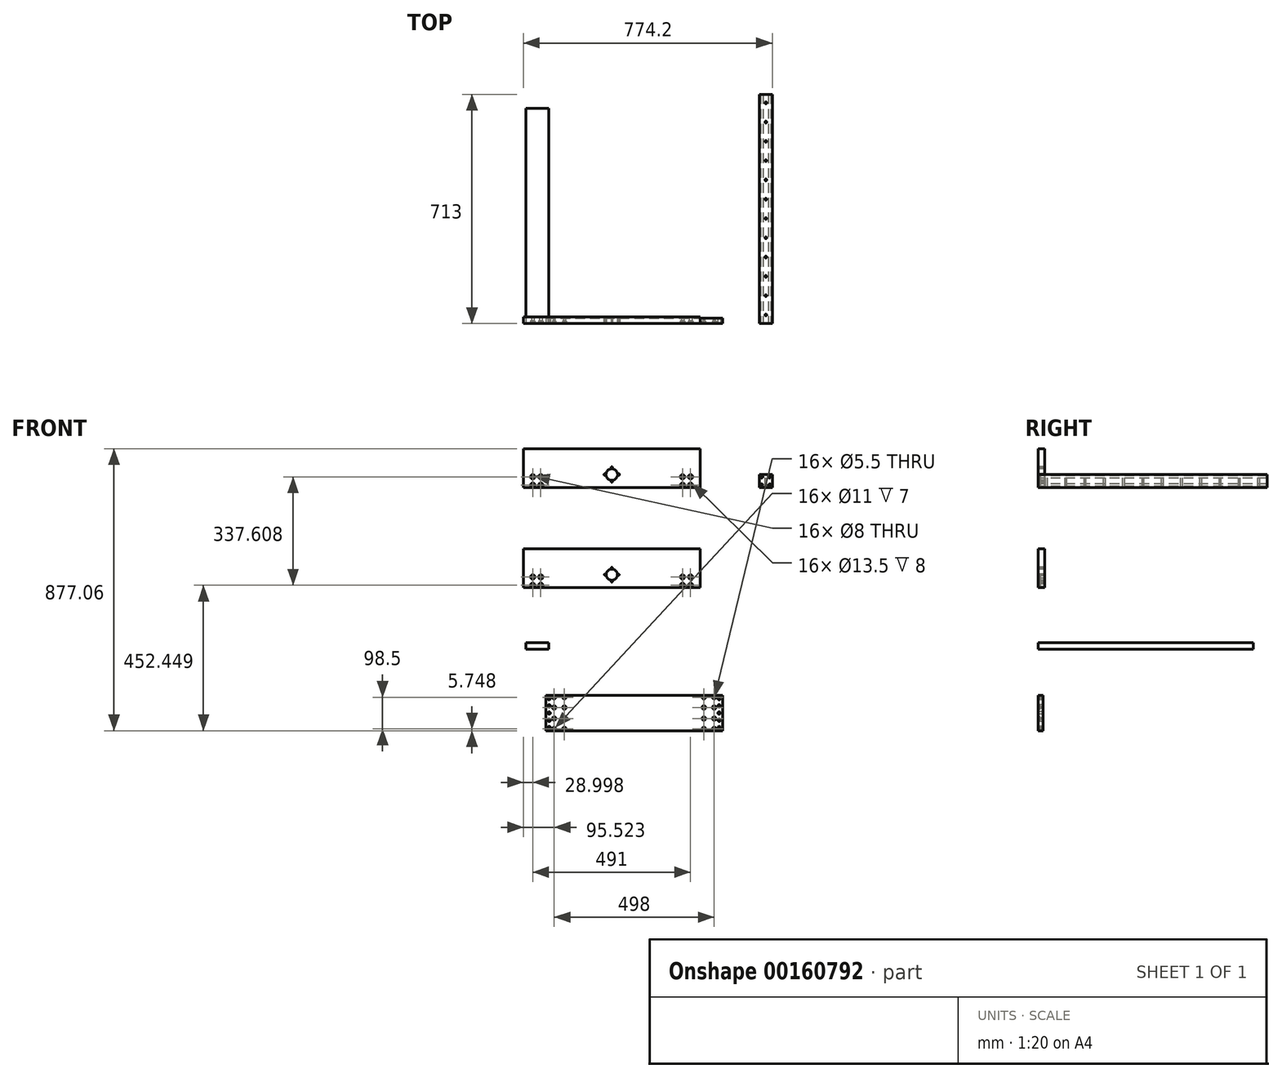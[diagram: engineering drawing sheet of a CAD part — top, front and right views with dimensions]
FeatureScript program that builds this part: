
annotation { "Feature Type Name" : "Feature", "Feature Type Description" : "" }
export const myFeature = defineFeature(function(context is Context, id is Id, definition is map)
    precondition{}
    {
        {
            var Q0;
            Q0=qCreatedBy(makeId("Front.planeOp"),FACE);
            var sketch = newSketch(context, id + "F0", { "sketchPlane" : qUnion([Q0])});
            skLineSegment(sketch, "E0.bottom", {"start": v(-1050.56, 346.5) * mm, "end": v(-500.56, 346.5) * mm});
            skLineSegment(sketch, "E0.top", {"start": v(-1050.56, 226.5) * mm, "end": v(-500.56, 226.5) * mm});
            skLineSegment(sketch, "E0.left", {"start": v(-1050.56, 346.5) * mm, "end": v(-1050.56, 226.5) * mm});
            skLineSegment(sketch, "E0.right", {"start": v(-500.56, 346.5) * mm, "end": v(-500.56, 226.5) * mm});
            skLineSegment(sketch, "E1.bottom", {"start": v(-316.36, 266.5) * mm, "end": v(-276.36, 266.5) * mm});
            skLineSegment(sketch, "E1.top", {"start": v(-316.36, 226.5) * mm, "end": v(-276.36, 226.5) * mm});
            skLineSegment(sketch, "E1.left", {"start": v(-316.36, 266.5) * mm, "end": v(-316.36, 226.5) * mm});
            skLineSegment(sketch, "E1.right", {"start": v(-276.36, 266.5) * mm, "end": v(-276.36, 226.5) * mm});
            skCircle(sketch, "E2", {"center": v(-309.36, 259.5) * mm, "radius": 4 * mm});
            skCircle(sketch, "E3.0.1.0", {"center": v(-309.36, 233.5) * mm, "radius": 4 * mm});
            skCircle(sketch, "E3.1.0.0", {"center": v(-284.36, 259.5) * mm, "radius": 4 * mm});
            skCircle(sketch, "E3.1.1.0", {"center": v(-284.36, 233.5) * mm, "radius": 4 * mm});
            skLineSegment(sketch, "E3.direction1", {"start": v(-309.36, 259.5) * mm, "end": v(-284.36, 259.5) * mm, "construction": true});
            skLineSegment(sketch, "E3.direction2", {"start": v(-309.36, 259.5) * mm, "end": v(-309.36, 233.5) * mm, "construction": true});
            skCircle(sketch, "E4.1.1.0", {"center": v(-142.75, 136.48) * mm, "radius": 4 * mm});
            skLineSegment(sketch, "E5.0", {"start": v(-1028.56, 346.5) * mm, "end": v(-1028.56, 226.5) * mm, "construction": true});
            skLineSegment(sketch, "E6.0", {"start": v(-522.56, 346.5) * mm, "end": v(-522.56, 226.5) * mm, "construction": true});
            skLineSegment(sketch, "E7.0", {"start": v(-1050.56, 266.5) * mm, "end": v(-500.56, 266.5) * mm, "construction": true});
            skLineSegment(sketch, "E8.bottom", {"start": v(-1028.56, 266.5) * mm, "end": v(-988.56, 266.5) * mm, "construction": true});
            skLineSegment(sketch, "E8.top", {"start": v(-1028.56, 226.5) * mm, "end": v(-988.56, 226.5) * mm, "construction": true});
            skLineSegment(sketch, "E8.left", {"start": v(-1028.56, 266.5) * mm, "end": v(-1028.56, 226.5) * mm, "construction": true});
            skLineSegment(sketch, "E8.right", {"start": v(-988.56, 266.5) * mm, "end": v(-988.56, 226.5) * mm, "construction": true});
            skCircle(sketch, "E9", {"center": v(-1021.56, 259.5) * mm, "radius": 4 * mm, "construction": true});
            skCircle(sketch, "E10.0.1.0", {"center": v(-1021.56, 233.5) * mm, "radius": 4 * mm, "construction": true});
            skCircle(sketch, "E10.1.0.0", {"center": v(-996.56, 259.5) * mm, "radius": 4 * mm, "construction": true});
            skCircle(sketch, "E10.1.1.0", {"center": v(-996.56, 233.5) * mm, "radius": 4 * mm, "construction": true});
            skLineSegment(sketch, "E10.direction1", {"start": v(-1021.56, 259.5) * mm, "end": v(-996.56, 259.5) * mm, "construction": true});
            skLineSegment(sketch, "E10.direction2", {"start": v(-1021.56, 259.5) * mm, "end": v(-1021.56, 233.5) * mm, "construction": true});
            skLineSegment(sketch, "E11.bottom", {"start": v(-562.56, 266.5) * mm, "end": v(-522.56, 266.5) * mm, "construction": true});
            skLineSegment(sketch, "E11.top", {"start": v(-562.56, 226.5) * mm, "end": v(-522.56, 226.5) * mm, "construction": true});
            skLineSegment(sketch, "E11.left", {"start": v(-562.56, 266.5) * mm, "end": v(-562.56, 226.5) * mm, "construction": true});
            skLineSegment(sketch, "E11.right", {"start": v(-522.56, 266.5) * mm, "end": v(-522.56, 226.5) * mm, "construction": true});
            skCircle(sketch, "E12", {"center": v(-555.56, 259.5) * mm, "radius": 4 * mm, "construction": true});
            skCircle(sketch, "E13.0.1.0", {"center": v(-555.56, 233.5) * mm, "radius": 4 * mm, "construction": true});
            skCircle(sketch, "E13.1.0.0", {"center": v(-530.56, 259.5) * mm, "radius": 4 * mm, "construction": true});
            skCircle(sketch, "E13.1.1.0", {"center": v(-530.56, 233.5) * mm, "radius": 4 * mm, "construction": true});
            skLineSegment(sketch, "E13.direction1", {"start": v(-555.56, 259.5) * mm, "end": v(-530.56, 259.5) * mm, "construction": true});
            skLineSegment(sketch, "E13.direction2", {"start": v(-555.56, 259.5) * mm, "end": v(-555.56, 233.5) * mm, "construction": true});
            skLineSegment(sketch, "E14.bottom", {"start": v(-1050.56, 34.9) * mm, "end": v(-500.56, 34.9) * mm});
            skLineSegment(sketch, "E14.top", {"start": v(-1050.56, -85.1) * mm, "end": v(-500.56, -85.1) * mm});
            skLineSegment(sketch, "E14.left", {"start": v(-1050.56, 34.9) * mm, "end": v(-1050.56, -85.1) * mm});
            skLineSegment(sketch, "E14.right", {"start": v(-500.56, 34.9) * mm, "end": v(-500.56, -85.1) * mm});
            skLineSegment(sketch, "E15.0", {"start": v(-1028.56, 34.9) * mm, "end": v(-1028.56, -85.1) * mm, "construction": true});
            skLineSegment(sketch, "E16.0", {"start": v(-522.56, 34.9) * mm, "end": v(-522.56, -85.1) * mm, "construction": true});
            skLineSegment(sketch, "E17.0", {"start": v(-1050.56, -45.1) * mm, "end": v(-500.56, -45.1) * mm, "construction": true});
            skLineSegment(sketch, "E18.bottom", {"start": v(-1028.56, -45.1) * mm, "end": v(-988.56, -45.1) * mm, "construction": true});
            skLineSegment(sketch, "E18.top", {"start": v(-1028.56, -85.1) * mm, "end": v(-988.56, -85.1) * mm, "construction": true});
            skLineSegment(sketch, "E18.left", {"start": v(-1028.56, -45.1) * mm, "end": v(-1028.56, -85.1) * mm, "construction": true});
            skLineSegment(sketch, "E18.right", {"start": v(-988.56, -45.1) * mm, "end": v(-988.56, -85.1) * mm, "construction": true});
            skCircle(sketch, "E19", {"center": v(-1021.56, -52.1) * mm, "radius": 4 * mm, "construction": true});
            skCircle(sketch, "E20.0.1.0", {"center": v(-1021.56, -78.1) * mm, "radius": 4 * mm, "construction": true});
            skCircle(sketch, "E20.1.0.0", {"center": v(-996.56, -52.1) * mm, "radius": 4 * mm, "construction": true});
            skCircle(sketch, "E20.1.1.0", {"center": v(-996.56, -78.1) * mm, "radius": 4 * mm, "construction": true});
            skLineSegment(sketch, "E20.direction1", {"start": v(-1021.56, -52.1) * mm, "end": v(-996.56, -52.1) * mm, "construction": true});
            skLineSegment(sketch, "E20.direction2", {"start": v(-1021.56, -52.1) * mm, "end": v(-1021.56, -78.1) * mm, "construction": true});
            skLineSegment(sketch, "E21.bottom", {"start": v(-562.56, -45.1) * mm, "end": v(-522.56, -45.1) * mm, "construction": true});
            skLineSegment(sketch, "E21.top", {"start": v(-562.56, -85.1) * mm, "end": v(-522.56, -85.1) * mm, "construction": true});
            skLineSegment(sketch, "E21.left", {"start": v(-562.56, -45.1) * mm, "end": v(-562.56, -85.1) * mm, "construction": true});
            skLineSegment(sketch, "E21.right", {"start": v(-522.56, -45.1) * mm, "end": v(-522.56, -85.1) * mm, "construction": true});
            skCircle(sketch, "E22", {"center": v(-555.56, -52.1) * mm, "radius": 4 * mm, "construction": true});
            skCircle(sketch, "E23.0.1.0", {"center": v(-555.56, -78.1) * mm, "radius": 4 * mm, "construction": true});
            skCircle(sketch, "E23.1.0.0", {"center": v(-530.56, -52.1) * mm, "radius": 4 * mm, "construction": true});
            skCircle(sketch, "E23.1.1.0", {"center": v(-530.56, -78.1) * mm, "radius": 4 * mm, "construction": true});
            skLineSegment(sketch, "E23.direction1", {"start": v(-555.56, -52.1) * mm, "end": v(-530.56, -52.1) * mm, "construction": true});
            skLineSegment(sketch, "E23.direction2", {"start": v(-555.56, -52.1) * mm, "end": v(-555.56, -78.1) * mm, "construction": true});
            skLineSegment(sketch, "E24.bottom", {"start": v(-1042.35, -257.26) * mm, "end": v(-972.35, -257.26) * mm});
            skLineSegment(sketch, "E24.top", {"start": v(-1042.35, -277.26) * mm, "end": v(-972.35, -277.26) * mm});
            skLineSegment(sketch, "E24.left", {"start": v(-1042.35, -257.26) * mm, "end": v(-1042.35, -277.26) * mm});
            skLineSegment(sketch, "E24.right", {"start": v(-972.35, -257.26) * mm, "end": v(-972.35, -277.26) * mm});
            skCircle(sketch, "E25", {"center": v(-1032.35, -267.26) * mm, "radius": 4.21 * mm, "construction": true});
            skCircle(sketch, "E26.1.0.0", {"center": v(-1007.35, -267.26) * mm, "radius": 4.21 * mm, "construction": true});
            skCircle(sketch, "E26.2.0.0", {"center": v(-982.35, -267.26) * mm, "radius": 4.21 * mm, "construction": true});
            skLineSegment(sketch, "E26.direction1", {"start": v(-1032.35, -267.26) * mm, "end": v(-1007.35, -267.26) * mm, "construction": true});
            skLineSegment(sketch, "E27", {"start": v(-775.56, 226.5) * mm, "end": v(-775.56, 346.5) * mm, "construction": true});
            skLineSegment(sketch, "E28", {"start": v(-753.56, 266.5) * mm, "end": v(-775.56, 266.5) * mm, "construction": true});
            skCircle(sketch, "E29", {"center": v(-775.56, 266.5) * mm, "radius": 22 * mm, "construction": true});
            skCircle(sketch, "E30", {"center": v(-753.56, 266.5) * mm, "radius": 2.25 * mm});
            skCircle(sketch, "E31.1.0", {"center": v(-775.56, 288.5) * mm, "radius": 2.25 * mm});
            skCircle(sketch, "E31.2.0", {"center": v(-797.56, 266.5) * mm, "radius": 2.25 * mm});
            skCircle(sketch, "E31.3.0", {"center": v(-775.56, 244.5) * mm, "radius": 2.25 * mm});
            skLineSegment(sketch, "E32", {"start": v(-757.56, 266.5) * mm, "end": v(-775.56, 266.5) * mm, "construction": true});
            skCircle(sketch, "E33", {"center": v(-775.56, 266.5) * mm, "radius": 18 * mm});
            skCircle(sketch, "E34", {"center": v(-775.56, 266.5) * mm, "radius": 8.65 * mm, "construction": true});
            skLineSegment(sketch, "E35", {"start": v(-775.56, 34.9) * mm, "end": v(-775.56, -85.1) * mm, "construction": true});
            skLineSegment(sketch, "E36", {"start": v(-775.56, -24.1) * mm, "end": v(-775.56, -45.1) * mm, "construction": true});
            skLineSegment(sketch, "E37", {"start": v(-792.96, -45.1) * mm, "end": v(-775.56, -45.1) * mm, "construction": true});
            skCircle(sketch, "E38", {"center": v(-775.56, -45.1) * mm, "radius": 21 * mm, "construction": true});
            skCircle(sketch, "E39", {"center": v(-775.56, -45.1) * mm, "radius": 17.4 * mm});
            skCircle(sketch, "E40", {"center": v(-775.56, -24.1) * mm, "radius": 2.25 * mm, "construction": true});
            skCircle(sketch, "E41.1.0", {"center": v(-796.56, -45.1) * mm, "radius": 2.25 * mm, "construction": true});
            skCircle(sketch, "E41.2.0", {"center": v(-775.56, -66.1) * mm, "radius": 2.25 * mm, "construction": true});
            skCircle(sketch, "E41.3.0", {"center": v(-754.56, -45.1) * mm, "radius": 2.25 * mm, "construction": true});
            skLineSegment(sketch, "E42.bottom", {"start": v(-981.04, -420.55) * mm, "end": v(-431.04, -420.55) * mm});
            skLineSegment(sketch, "E42.top", {"start": v(-981.04, -530.55) * mm, "end": v(-431.04, -530.55) * mm});
            skLineSegment(sketch, "E42.left", {"start": v(-981.04, -420.55) * mm, "end": v(-981.04, -530.55) * mm});
            skLineSegment(sketch, "E42.right", {"start": v(-431.04, -420.55) * mm, "end": v(-431.04, -530.55) * mm});
            skLineSegment(sketch, "E43.bottom", {"start": v(-918.04, -542.05) * mm, "end": v(-918.04, -475.55) * mm, "construction": true});
            skLineSegment(sketch, "E43.top", {"start": v(-960.04, -542.05) * mm, "end": v(-960.04, -475.55) * mm, "construction": true});
            skLineSegment(sketch, "E43.right", {"start": v(-918.04, -475.55) * mm, "end": v(-960.04, -475.55) * mm, "construction": true});
            skPoint(sketch, "E43.middle", {"position": v(-939.04, -508.8) * mm});
            skLineSegment(sketch, "E44.bottom", {"start": v(-955.04, -524.8) * mm, "end": v(-955.04, -492.8) * mm, "construction": true});
            skLineSegment(sketch, "E44.top", {"start": v(-923.04, -524.8) * mm, "end": v(-923.04, -492.8) * mm, "construction": true});
            skLineSegment(sketch, "E44.left", {"start": v(-955.04, -524.8) * mm, "end": v(-923.04, -524.8) * mm, "construction": true});
            skLineSegment(sketch, "E44.right", {"start": v(-955.04, -492.8) * mm, "end": v(-923.04, -492.8) * mm, "construction": true});
            skLineSegment(sketch, "E45", {"start": v(-918.04, -542.05) * mm, "end": v(-960.04, -542.05) * mm, "construction": true});
            skCircle(sketch, "E46", {"center": v(-923.04, -524.8) * mm, "radius": 2.75 * mm, "construction": true});
            skCircle(sketch, "E47.1.0", {"center": v(-923.04, -492.8) * mm, "radius": 2.75 * mm, "construction": true});
            skCircle(sketch, "E47.2.0", {"center": v(-955.04, -492.8) * mm, "radius": 2.75 * mm, "construction": true});
            skCircle(sketch, "E47.3.0", {"center": v(-955.04, -524.8) * mm, "radius": 2.75 * mm, "construction": true});
            skLineSegment(sketch, "E48.bottom", {"start": v(-918.04, -475.55) * mm, "end": v(-918.04, -409.05) * mm, "construction": true});
            skLineSegment(sketch, "E48.top", {"start": v(-960.04, -475.55) * mm, "end": v(-960.04, -409.05) * mm, "construction": true});
            skLineSegment(sketch, "E48.right", {"start": v(-918.04, -409.05) * mm, "end": v(-960.04, -409.05) * mm, "construction": true});
            skPoint(sketch, "E48.middle", {"position": v(-939.04, -442.3) * mm});
            skLineSegment(sketch, "E49.bottom", {"start": v(-955.04, -458.3) * mm, "end": v(-955.04, -426.3) * mm, "construction": true});
            skLineSegment(sketch, "E49.top", {"start": v(-923.04, -458.3) * mm, "end": v(-923.04, -426.3) * mm, "construction": true});
            skLineSegment(sketch, "E49.left", {"start": v(-955.04, -458.3) * mm, "end": v(-923.04, -458.3) * mm, "construction": true});
            skLineSegment(sketch, "E49.right", {"start": v(-955.04, -426.3) * mm, "end": v(-923.04, -426.3) * mm, "construction": true});
            skCircle(sketch, "E50", {"center": v(-923.04, -458.3) * mm, "radius": 2.75 * mm, "construction": true});
            skCircle(sketch, "E51.1.0", {"center": v(-923.04, -426.3) * mm, "radius": 2.75 * mm, "construction": true});
            skCircle(sketch, "E51.2.0", {"center": v(-955.04, -426.3) * mm, "radius": 2.75 * mm, "construction": true});
            skCircle(sketch, "E51.3.0", {"center": v(-955.04, -458.3) * mm, "radius": 2.75 * mm, "construction": true});
            skLineSegment(sketch, "E52", {"start": v(-706.04, -530.55) * mm, "end": v(-706.04, -420.55) * mm, "construction": true});
            skLineSegment(sketch, "E53.0", {"start": v(-452.04, -530.55) * mm, "end": v(-452.04, -420.55) * mm, "construction": true});
            skLineSegment(sketch, "E54.0", {"start": v(-960.04, -530.55) * mm, "end": v(-960.04, -420.55) * mm, "construction": true});
            skLineSegment(sketch, "E55", {"start": v(-981.04, -475.55) * mm, "end": v(-431.04, -475.55) * mm, "construction": true});
            skLineSegment(sketch, "E56.bottom", {"start": v(-452.04, -542.05) * mm, "end": v(-452.04, -475.55) * mm, "construction": true});
            skLineSegment(sketch, "E56.top", {"start": v(-494.04, -542.05) * mm, "end": v(-494.04, -475.55) * mm, "construction": true});
            skLineSegment(sketch, "E56.right", {"start": v(-452.04, -475.55) * mm, "end": v(-494.04, -475.55) * mm, "construction": true});
            skPoint(sketch, "E56.middle", {"position": v(-473.04, -508.8) * mm});
            skLineSegment(sketch, "E57.bottom", {"start": v(-489.04, -524.8) * mm, "end": v(-489.04, -492.8) * mm, "construction": true});
            skLineSegment(sketch, "E57.top", {"start": v(-457.04, -524.8) * mm, "end": v(-457.04, -492.8) * mm, "construction": true});
            skLineSegment(sketch, "E57.left", {"start": v(-489.04, -524.8) * mm, "end": v(-457.04, -524.8) * mm, "construction": true});
            skLineSegment(sketch, "E57.right", {"start": v(-489.04, -492.8) * mm, "end": v(-457.04, -492.8) * mm, "construction": true});
            skLineSegment(sketch, "E58", {"start": v(-452.04, -542.05) * mm, "end": v(-494.04, -542.05) * mm, "construction": true});
            skCircle(sketch, "E59", {"center": v(-457.04, -524.8) * mm, "radius": 2.75 * mm, "construction": true});
            skCircle(sketch, "E60.1.0", {"center": v(-457.04, -492.8) * mm, "radius": 2.75 * mm, "construction": true});
            skCircle(sketch, "E60.2.0", {"center": v(-489.04, -492.8) * mm, "radius": 2.75 * mm, "construction": true});
            skCircle(sketch, "E60.3.0", {"center": v(-489.04, -524.8) * mm, "radius": 2.75 * mm, "construction": true});
            skLineSegment(sketch, "E61.bottom", {"start": v(-452.04, -475.55) * mm, "end": v(-452.04, -409.05) * mm, "construction": true});
            skLineSegment(sketch, "E61.top", {"start": v(-494.04, -475.55) * mm, "end": v(-494.04, -409.05) * mm, "construction": true});
            skLineSegment(sketch, "E61.right", {"start": v(-452.04, -409.05) * mm, "end": v(-494.04, -409.05) * mm, "construction": true});
            skPoint(sketch, "E61.middle", {"position": v(-473.04, -442.3) * mm});
            skLineSegment(sketch, "E62.bottom", {"start": v(-489.04, -458.3) * mm, "end": v(-489.04, -426.3) * mm, "construction": true});
            skLineSegment(sketch, "E62.top", {"start": v(-457.04, -458.3) * mm, "end": v(-457.04, -426.3) * mm, "construction": true});
            skLineSegment(sketch, "E62.left", {"start": v(-489.04, -458.3) * mm, "end": v(-457.04, -458.3) * mm, "construction": true});
            skLineSegment(sketch, "E62.right", {"start": v(-489.04, -426.3) * mm, "end": v(-457.04, -426.3) * mm, "construction": true});
            skCircle(sketch, "E63", {"center": v(-457.04, -458.3) * mm, "radius": 2.75 * mm, "construction": true});
            skCircle(sketch, "E64.1.0", {"center": v(-457.04, -426.3) * mm, "radius": 2.75 * mm, "construction": true});
            skCircle(sketch, "E64.2.0", {"center": v(-489.04, -426.3) * mm, "radius": 2.75 * mm, "construction": true});
            skCircle(sketch, "E64.3.0", {"center": v(-489.04, -458.3) * mm, "radius": 2.75 * mm, "construction": true});
            skCircle(sketch, "E65", {"center": v(-970.54, -520.55) * mm, "radius": 4.37 * mm, "construction": true});
            skCircle(sketch, "E66.0.1.0", {"center": v(-970.54, -498.05) * mm, "radius": 4.37 * mm, "construction": true});
            skCircle(sketch, "E66.0.2.0", {"center": v(-970.54, -475.55) * mm, "radius": 4.37 * mm, "construction": true});
            skCircle(sketch, "E66.0.3.0", {"center": v(-970.54, -453.05) * mm, "radius": 4.37 * mm, "construction": true});
            skCircle(sketch, "E66.0.4.0", {"center": v(-970.54, -430.55) * mm, "radius": 4.37 * mm, "construction": true});
            skLineSegment(sketch, "E66.direction1", {"start": v(-997.8, -520.55) * mm, "end": v(-970.54, -520.55) * mm, "construction": true});
            skLineSegment(sketch, "E66.direction2", {"start": v(-970.54, -520.55) * mm, "end": v(-970.54, -498.05) * mm, "construction": true});
            skCircle(sketch, "E67", {"center": v(-441.54, -520.55) * mm, "radius": 4.32 * mm, "construction": true});
            skCircle(sketch, "E68.0.1.0", {"center": v(-441.54, -498.05) * mm, "radius": 4.32 * mm, "construction": true});
            skCircle(sketch, "E68.0.2.0", {"center": v(-441.54, -475.55) * mm, "radius": 4.32 * mm, "construction": true});
            skCircle(sketch, "E68.0.3.0", {"center": v(-441.54, -453.05) * mm, "radius": 4.32 * mm, "construction": true});
            skCircle(sketch, "E68.0.4.0", {"center": v(-441.54, -430.55) * mm, "radius": 4.32 * mm, "construction": true});
            skLineSegment(sketch, "E68.direction1", {"start": v(-441.54, -520.55) * mm, "end": v(-416.54, -520.55) * mm, "construction": true});
            skLineSegment(sketch, "E68.direction2", {"start": v(-441.54, -520.55) * mm, "end": v(-441.54, -498.05) * mm, "construction": true});
            skLineSegment(sketch, "E69.bottom", {"start": v(-117.08, -509.78) * mm, "end": v(-227.08, -509.78) * mm});
            skLineSegment(sketch, "E69.top", {"start": v(-117.08, -109.78) * mm, "end": v(-227.08, -109.78) * mm});
            skLineSegment(sketch, "E69.left", {"start": v(-117.08, -509.78) * mm, "end": v(-117.08, -109.78) * mm});
            skLineSegment(sketch, "E69.right", {"start": v(-227.08, -509.78) * mm, "end": v(-227.08, -109.78) * mm});
            skPoint(sketch, "E69.middle", {"position": v(-172.08, -309.78) * mm});
            skLineSegment(sketch, "E70.0", {"start": v(-117.08, -457.78) * mm, "end": v(-227.08, -457.78) * mm, "construction": true});
            skLineSegment(sketch, "E71.0", {"start": v(-117.08, -437.78) * mm, "end": v(-177.08, -437.78) * mm, "construction": true});
            skLineSegment(sketch, "E72.0", {"start": v(-177.08, -437.78) * mm, "end": v(-177.08, -109.78) * mm, "construction": true});
            skLineSegment(sketch, "E73.0", {"start": v(-117.08, -277.78) * mm, "end": v(-227.08, -277.78) * mm, "construction": true});
            skLineSegment(sketch, "E74.filletArc", {"start": v(-177.08, -437.78) * mm, "end": v(-177.08, -437.78) * mm});
            skLineSegment(sketch, "E75.0", {"start": v(-117.08, -257.78) * mm, "end": v(-227.08, -257.78) * mm});
            skLineSegment(sketch, "E76.0", {"start": v(-117.08, -129.78) * mm, "end": v(-227.08, -129.78) * mm});
            skSolve(sketch);
        }
        {
            var Q0;
            Q0=makeQuery(id+"F0.imprint","IMPRINT",FACE,{"disambiguationData":[TD([[makeQuery(id+"F0.imprint","IMPRINT",EDGE,{"derivedFrom":sQuery(id+"F0.wireOp",EDGE,"E0.bottom")}),-1.0]])]});
            extrude(context, id + "F1", {"entities" : qUnion([Q0]), "oppositeDirection" : true, "depth" : 20 * mm});
        }
        {
            var Q0;
            Q0=makeQuery(id+"F0.imprint","IMPRINT",FACE,{"disambiguationData":[TD([[makeQuery(id+"F0.imprint","IMPRINT",EDGE,{"derivedFrom":sQuery(id+"F0.wireOp",EDGE,"E2")}),1.0]])]});
            var Q1;
            Q1=makeQuery(id+"F0.imprint","IMPRINT",FACE,{"disambiguationData":[TD([[makeQuery(id+"F0.imprint","IMPRINT",EDGE,{"derivedFrom":sQuery(id+"F0.wireOp",EDGE,"E3.0.1.0")}),1.0]])]});
            var Q2;
            Q2=makeQuery(id+"F0.imprint","IMPRINT",FACE,{"disambiguationData":[TD([[makeQuery(id+"F0.imprint","IMPRINT",EDGE,{"derivedFrom":sQuery(id+"F0.wireOp",EDGE,"E3.1.0.0")}),1.0]])]});
            var Q3;
            Q3=makeQuery(id+"F0.imprint","IMPRINT",FACE,{"disambiguationData":[TD([[makeQuery(id+"F0.imprint","IMPRINT",EDGE,{"derivedFrom":sQuery(id+"F0.wireOp",EDGE,"E3.1.1.0")}),1.0]])]});
            var Q4;
            Q4=makeQuery(id+"F0.imprint","IMPRINT",FACE,{"disambiguationData":[TD([[makeQuery(id+"F0.imprint","IMPRINT",EDGE,{"derivedFrom":sQuery(id+"F0.wireOp",EDGE,"E1.bottom")}),-1.0]])]});
            extrude(context, id + "F2", {"entities" : qUnion([Q0, Q1, Q2, Q3, Q4]), "oppositeDirection" : true, "depth" : 713 * mm});
        }
        {
            var Q0;
            Q0=makeQuery(id+"F0.imprint","IMPRINT",FACE,{"disambiguationData":[TD([[makeQuery(id+"F0.imprint","IMPRINT",EDGE,{"derivedFrom":sQuery(id+"F0.wireOp",EDGE,"E14.bottom")}),-1.0]])]});
            extrude(context, id + "F3", {"entities" : qUnion([Q0]), "oppositeDirection" : true, "depth" : 20 * mm});
        }
        {
            var Q0;
            Q0=makeQuery(id+"F0.imprint","IMPRINT",FACE,{"disambiguationData":[TD([[makeQuery(id+"F0.imprint","IMPRINT",EDGE,{"derivedFrom":sQuery(id+"F0.wireOp",EDGE,"E24.bottom")}),-1.0]])]});
            extrude(context, id + "F4", {"entities" : qUnion([Q0]), "oppositeDirection" : true, "depth" : 669.8 * mm});
        }
        {
            var Q0;
            Q0=makeQuery(id+"F0.imprint","IMPRINT",FACE,{"disambiguationData":[TD([[makeQuery(id+"F0.imprint","IMPRINT",EDGE,{"derivedFrom":sQuery(id+"F0.wireOp",EDGE,"E42.bottom")}),-1.0]])]});
            extrude(context, id + "F5", {"entities" : qUnion([Q0]), "oppositeDirection" : true, "depth" : 16 * mm});
        }
        {
            var Q0;
            Q0=makeQuery(id+"F2.opExtrude","SWEPT_FACE",FACE,{"disambiguationData":[OSD([sQuery(id+"F0.wireOp",EDGE,"E1.bottom")])]});
            var sketch = newSketch(context, id + "F6", { "sketchPlane" : qUnion([Q0])});
            skLineSegment(sketch, "E77.0", {"start": v(-316.36, 26.5) * mm, "end": v(-276.36, 26.5) * mm, "construction": true});
            skCircle(sketch, "E78", {"center": v(-296.36, 26.5) * mm, "radius": 6.1 * mm, "construction": true});
            skCircle(sketch, "E79.0.1.0", {"center": v(-296.36, 86.5) * mm, "radius": 6.1 * mm, "construction": true});
            skCircle(sketch, "E79.0.2.0", {"center": v(-296.36, 146.5) * mm, "radius": 6.1 * mm, "construction": true});
            skCircle(sketch, "E79.0.3.0", {"center": v(-296.36, 206.5) * mm, "radius": 6.1 * mm, "construction": true});
            skCircle(sketch, "E79.0.4.0", {"center": v(-296.36, 266.5) * mm, "radius": 6.1 * mm, "construction": true});
            skCircle(sketch, "E79.0.5.0", {"center": v(-296.36, 326.5) * mm, "radius": 6.1 * mm, "construction": true});
            skCircle(sketch, "E79.0.6.0", {"center": v(-296.36, 386.5) * mm, "radius": 6.1 * mm, "construction": true});
            skCircle(sketch, "E79.0.7.0", {"center": v(-296.36, 446.5) * mm, "radius": 6.1 * mm, "construction": true});
            skCircle(sketch, "E79.0.8.0", {"center": v(-296.36, 506.5) * mm, "radius": 6.1 * mm, "construction": true});
            skCircle(sketch, "E79.0.9.0", {"center": v(-296.36, 566.5) * mm, "radius": 6.1 * mm, "construction": true});
            skCircle(sketch, "E79.0.10.0", {"center": v(-296.36, 626.5) * mm, "radius": 6.1 * mm, "construction": true});
            skLineSegment(sketch, "E79.direction1", {"start": v(-296.36, 26.5) * mm, "end": v(-271.36, 26.5) * mm, "construction": true});
            skLineSegment(sketch, "E79.direction2", {"start": v(-296.36, 26.5) * mm, "end": v(-296.36, 86.5) * mm, "construction": true});
            skCircle(sketch, "E80.0.0.11", {"center": v(-296.36, 686.5) * mm, "radius": 6.1 * mm, "construction": true});
            skSolve(sketch);
        }
        {
            var Q0;
            Q0=sQuery(id+"F0.wireOp",VERTEX,"E41.1.0.center");
            var Q1;
            Q1=sQuery(id+"F0.wireOp",VERTEX,"E36.start");
            var Q2;
            Q2=sQuery(id+"F0.wireOp",VERTEX,"E41.3.0.center");
            var Q3;
            Q3=sQuery(id+"F0.wireOp",VERTEX,"E41.2.0.center");
            var Q4;
            Q4=makeQuery(id+"F3.opExtrude","SWEPT_BODY",BODY,{"disambiguationData":[OSD([sQuery(id+"F0.wireOp",EDGE,"E14.bottom"),sQuery(id+"F0.wireOp",EDGE,"E14.top"),sQuery(id+"F0.wireOp",EDGE,"E14.left"),sQuery(id+"F0.wireOp",EDGE,"E14.right"),sQuery(id+"F0.wireOp",EDGE,"E39")])]});
            hole(context, id + "F7", {"style" : HoleStyle.SIMPLE, "endStyle" : HoleEndStyle.THROUGH, "holeDiameter" : 4.2 * mm, "locations" : qUnion([Q0, Q1, Q2, Q3]), "scope" : qUnion([Q4]), "isTappedThrough" : true});
        }
        {
            var Q0;
            Q0=sQuery(id+"F0.wireOp",VERTEX,"E9.center");
            var Q1;
            Q1=sQuery(id+"F0.wireOp",VERTEX,"E10.1.0.0.center");
            var Q2;
            Q2=sQuery(id+"F0.wireOp",VERTEX,"E10.1.1.0.center");
            var Q3;
            Q3=sQuery(id+"F0.wireOp",VERTEX,"E10.0.1.0.center");
            var Q4;
            Q4=sQuery(id+"F0.wireOp",VERTEX,"E12.center");
            var Q5;
            Q5=sQuery(id+"F0.wireOp",VERTEX,"E13.0.1.0.center");
            var Q6;
            Q6=sQuery(id+"F0.wireOp",VERTEX,"E13.1.1.0.center");
            var Q7;
            Q7=sQuery(id+"F0.wireOp",VERTEX,"E13.1.0.0.center");
            var Q8;
            Q8=sQuery(id+"F0.wireOp",VERTEX,"E20.direction1.start");
            var Q9;
            Q9=sQuery(id+"F0.wireOp",VERTEX,"E20.direction1.end");
            var Q10;
            Q10=sQuery(id+"F0.wireOp",VERTEX,"E20.1.1.0.center");
            var Q11;
            Q11=sQuery(id+"F0.wireOp",VERTEX,"E20.0.1.0.center");
            var Q12;
            Q12=sQuery(id+"F0.wireOp",VERTEX,"E22.center");
            var Q13;
            Q13=sQuery(id+"F0.wireOp",VERTEX,"E23.direction1.end");
            var Q14;
            Q14=sQuery(id+"F0.wireOp",VERTEX,"E23.1.1.0.center");
            var Q15;
            Q15=sQuery(id+"F0.wireOp",VERTEX,"E23.direction2.end");
            var Q16;
            Q16=sQuery(id+"F0.wireOp",VERTEX,"3d9f6cbd-3779-42ef-b97e-b74c730929e5.center");
            var Q17;
            Q17=sQuery(id+"F0.wireOp",VERTEX,"caae9ad1-e9a7-4160-9bcf-ab340074576d.1.0.0.center");
            var Q18;
            Q18=sQuery(id+"F0.wireOp",VERTEX,"caae9ad1-e9a7-4160-9bcf-ab340074576d.2.0.0.center");
            var Q19;
            Q19=makeQuery(id+"F1.opExtrude","SWEPT_BODY",BODY,{"disambiguationData":[OSD([sQuery(id+"F0.wireOp",EDGE,"E0.bottom"),sQuery(id+"F0.wireOp",EDGE,"E0.top"),sQuery(id+"F0.wireOp",EDGE,"E0.left"),sQuery(id+"F0.wireOp",EDGE,"E0.right")])]});
            var Q20;
            Q20=makeQuery(id+"F3.opExtrude","SWEPT_BODY",BODY,{"disambiguationData":[OSD([sQuery(id+"F0.wireOp",EDGE,"E14.bottom"),sQuery(id+"F0.wireOp",EDGE,"E14.top"),sQuery(id+"F0.wireOp",EDGE,"E14.left"),sQuery(id+"F0.wireOp",EDGE,"E14.right")])]});
            hole(context, id + "F8", {"style" : HoleStyle.C_BORE, "endStyle" : HoleEndStyle.THROUGH, "holeDiameter" : 8 * mm, "cBoreDiameter" : 13.5 * mm, "cBoreDepth" : 8 * mm, "locations" : qUnion([Q0, Q1, Q2, Q3, Q4, Q5, Q6, Q7, Q8, Q9, Q10, Q11, Q12, Q13, Q14, Q15, Q16, Q17, Q18]), "scope" : qUnion([Q19, Q20]), "isTappedThrough" : true});
        }
        {
            var Q0;
            Q0=sQuery(id+"F0.wireOp",VERTEX,"E3.direction2.end");
            var Q1;
            Q1=sQuery(id+"F0.wireOp",VERTEX,"E3.direction2.start");
            var Q2;
            Q2=sQuery(id+"F0.wireOp",VERTEX,"E3.direction1.end");
            var Q3;
            Q3=sQuery(id+"F0.wireOp",VERTEX,"E3.1.1.0.center");
            var Q4;
            Q4=makeQuery(id+"F2.opExtrude","SWEPT_BODY",BODY,{"disambiguationData":[OSD([sQuery(id+"F0.wireOp",EDGE,"E1.bottom"),sQuery(id+"F0.wireOp",EDGE,"E1.top"),sQuery(id+"F0.wireOp",EDGE,"E1.left"),sQuery(id+"F0.wireOp",EDGE,"E1.right")])]});
            hole(context, id + "F9", {"style" : HoleStyle.SIMPLE, "endStyle" : HoleEndStyle.THROUGH, "holeDiameter" : 7.6 * mm, "locations" : qUnion([Q0, Q1, Q2, Q3]), "scope" : qUnion([Q4]), "isTappedThrough" : true});
        }
        {
            var Q0;
            Q0=sQuery(id+"F6.wireOp",VERTEX,"E78.center");
            var Q1;
            Q1=sQuery(id+"F6.wireOp",VERTEX,"E79.0.1.0.center");
            var Q2;
            Q2=sQuery(id+"F6.wireOp",VERTEX,"E79.0.2.0.center");
            var Q3;
            Q3=sQuery(id+"F6.wireOp",VERTEX,"E79.0.3.0.center");
            var Q4;
            Q4=sQuery(id+"F6.wireOp",VERTEX,"E79.0.4.0.center");
            var Q5;
            Q5=sQuery(id+"F6.wireOp",VERTEX,"E79.0.5.0.center");
            var Q6;
            Q6=sQuery(id+"F6.wireOp",VERTEX,"E79.0.6.0.center");
            var Q7;
            Q7=sQuery(id+"F6.wireOp",VERTEX,"E79.0.7.0.center");
            var Q8;
            Q8=sQuery(id+"F6.wireOp",VERTEX,"E79.0.8.0.center");
            var Q9;
            Q9=sQuery(id+"F6.wireOp",VERTEX,"E79.0.9.0.center");
            var Q10;
            Q10=sQuery(id+"F6.wireOp",VERTEX,"E79.0.10.0.center");
            var Q11;
            Q11=sQuery(id+"F6.wireOp",VERTEX,"E78.center");
            var Q12;
            Q12=sQuery(id+"F6.wireOp",VERTEX,"E79.0.1.0.center");
            var Q13;
            Q13=sQuery(id+"F6.wireOp",VERTEX,"E79.0.2.0.center");
            var Q14;
            Q14=sQuery(id+"F6.wireOp",VERTEX,"E79.0.3.0.center");
            var Q15;
            Q15=sQuery(id+"F6.wireOp",VERTEX,"E79.0.4.0.center");
            var Q16;
            Q16=sQuery(id+"F6.wireOp",VERTEX,"E79.0.5.0.center");
            var Q17;
            Q17=sQuery(id+"F6.wireOp",VERTEX,"E79.0.6.0.center");
            var Q18;
            Q18=sQuery(id+"F6.wireOp",VERTEX,"E79.0.7.0.center");
            var Q19;
            Q19=sQuery(id+"F6.wireOp",VERTEX,"E79.0.8.0.center");
            var Q20;
            Q20=sQuery(id+"F6.wireOp",VERTEX,"E79.0.9.0.center");
            var Q21;
            Q21=sQuery(id+"F6.wireOp",VERTEX,"E79.0.10.0.center");
            var Q22;
            Q22=sQuery(id+"F6.wireOp",VERTEX,"E80.0.0.11.center");
            var Q23;
            Q23=makeQuery(id+"F4.opExtrude","SWEPT_BODY",BODY,{"disambiguationData":[OSD([sQuery(id+"F0.wireOp",EDGE,"E24.bottom"),sQuery(id+"F0.wireOp",EDGE,"E24.top"),sQuery(id+"F0.wireOp",EDGE,"E24.left"),sQuery(id+"F0.wireOp",EDGE,"E24.right")])]});
            var Q24;
            Q24=makeQuery(id+"F2.opExtrude","SWEPT_BODY",BODY,{"disambiguationData":[OSD([sQuery(id+"F0.wireOp",EDGE,"E1.bottom"),sQuery(id+"F0.wireOp",EDGE,"E1.top"),sQuery(id+"F0.wireOp",EDGE,"E1.left"),sQuery(id+"F0.wireOp",EDGE,"E1.right")])]});
            hole(context, id + "F10", {"style" : HoleStyle.SIMPLE, "endStyle" : HoleEndStyle.THROUGH, "holeDiameter" : 5.8 * mm, "locations" : qUnion([Q0, Q1, Q2, Q3, Q4, Q5, Q6, Q7, Q8, Q9, Q10, Q11, Q12, Q13, Q14, Q15, Q16, Q17, Q18, Q19, Q20, Q21, Q22]), "scope" : qUnion([Q23, Q24]), "isTappedThrough" : true});
        }
        {
            var Q0;
            Q0=sQuery(id+"F0.wireOp",VERTEX,"E49.bottom.start");
            var Q1;
            Q1=sQuery(id+"F0.wireOp",VERTEX,"E49.right.start");
            var Q2;
            Q2=sQuery(id+"F0.wireOp",VERTEX,"E49.right.end");
            var Q3;
            Q3=sQuery(id+"F0.wireOp",VERTEX,"E49.left.end");
            var Q4;
            Q4=sQuery(id+"F0.wireOp",VERTEX,"E47.1.0.center");
            var Q5;
            Q5=sQuery(id+"F0.wireOp",VERTEX,"E46.center");
            var Q6;
            Q6=sQuery(id+"F0.wireOp",VERTEX,"E47.2.0.center");
            var Q7;
            Q7=sQuery(id+"F0.wireOp",VERTEX,"E44.bottom.start");
            var Q8;
            Q8=sQuery(id+"F0.wireOp",VERTEX,"E62.right.start");
            var Q9;
            Q9=sQuery(id+"F0.wireOp",VERTEX,"E62.left.start");
            var Q10;
            Q10=sQuery(id+"F0.wireOp",VERTEX,"E57.right.start");
            var Q11;
            Q11=sQuery(id+"F0.wireOp",VERTEX,"E57.left.start");
            var Q12;
            Q12=sQuery(id+"F0.wireOp",VERTEX,"E57.left.end");
            var Q13;
            Q13=sQuery(id+"F0.wireOp",VERTEX,"E57.right.end");
            var Q14;
            Q14=sQuery(id+"F0.wireOp",VERTEX,"E63.center");
            var Q15;
            Q15=sQuery(id+"F0.wireOp",VERTEX,"E62.right.end");
            var Q16;
            Q16=makeQuery(id+"F5.opExtrude","SWEPT_BODY",BODY,{"disambiguationData":[OSD([sQuery(id+"F0.wireOp",EDGE,"E42.bottom"),sQuery(id+"F0.wireOp",EDGE,"E42.top"),sQuery(id+"F0.wireOp",EDGE,"E42.left"),sQuery(id+"F0.wireOp",EDGE,"E42.right")])]});
            hole(context, id + "F11", {"style" : HoleStyle.C_BORE, "endStyle" : HoleEndStyle.THROUGH, "holeDiameter" : 5.5 * mm, "cBoreDiameter" : 11 * mm, "cBoreDepth" : 7 * mm, "locations" : qUnion([Q0, Q1, Q2, Q3, Q4, Q5, Q6, Q7, Q8, Q9, Q10, Q11, Q12, Q13, Q14, Q15]), "scope" : qUnion([Q16]), "isTappedThrough" : true});
        }
        {
            var Q0;
            Q0=sQuery(id+"F0.wireOp",VERTEX,"E66.0.4.0.center");
            var Q1;
            Q1=sQuery(id+"F0.wireOp",VERTEX,"E66.0.3.0.center");
            var Q2;
            Q2=sQuery(id+"F0.wireOp",VERTEX,"E66.0.2.0.center");
            var Q3;
            Q3=sQuery(id+"F0.wireOp",VERTEX,"E66.direction2.end");
            var Q4;
            Q4=sQuery(id+"F0.wireOp",VERTEX,"E65.center");
            var Q5;
            Q5=sQuery(id+"F0.wireOp",VERTEX,"E68.direction1.start");
            var Q6;
            Q6=sQuery(id+"F0.wireOp",VERTEX,"E68.0.1.0.center");
            var Q7;
            Q7=sQuery(id+"F0.wireOp",VERTEX,"E68.0.2.0.center");
            var Q8;
            Q8=sQuery(id+"F0.wireOp",VERTEX,"E68.0.3.0.center");
            var Q9;
            Q9=sQuery(id+"F0.wireOp",VERTEX,"E68.0.4.0.center");
            var Q10;
            Q10=makeQuery(id+"F5.opExtrude","SWEPT_BODY",BODY,{"disambiguationData":[OSD([sQuery(id+"F0.wireOp",EDGE,"E42.bottom"),sQuery(id+"F0.wireOp",EDGE,"E42.top"),sQuery(id+"F0.wireOp",EDGE,"E42.left"),sQuery(id+"F0.wireOp",EDGE,"E42.right")])]});
            hole(context, id + "F12", {"style" : HoleStyle.SIMPLE, "endStyle" : HoleEndStyle.THROUGH, "holeDiameter" : 7.8 * mm, "locations" : qUnion([Q0, Q1, Q2, Q3, Q4, Q5, Q6, Q7, Q8, Q9]), "scope" : qUnion([Q10]), "isTappedThrough" : true});
        }
    });
